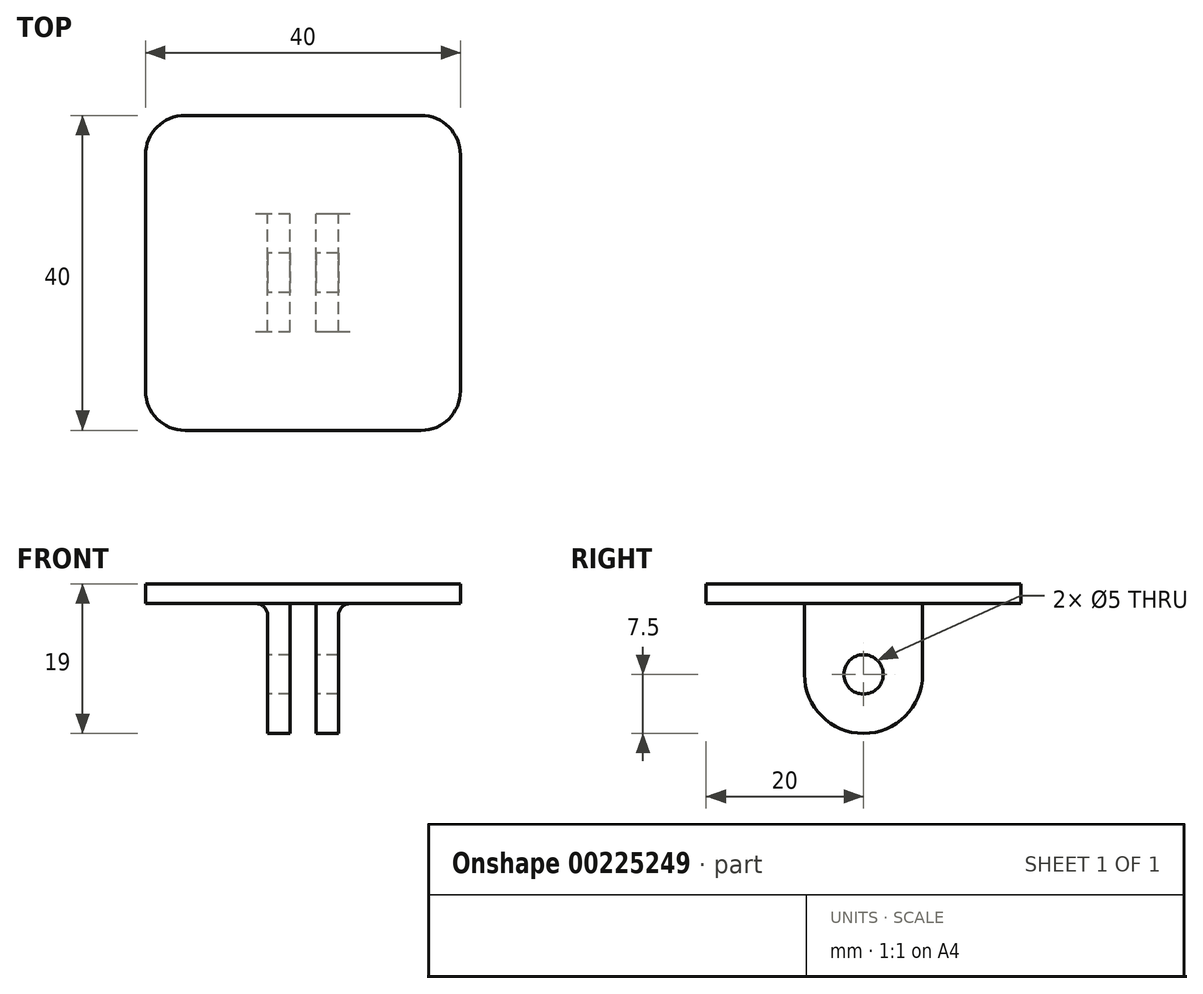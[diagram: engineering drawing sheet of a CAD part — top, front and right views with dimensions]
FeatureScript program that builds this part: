
annotation { "Feature Type Name" : "Feature", "Feature Type Description" : "" }
export const myFeature = defineFeature(function(context is Context, id is Id, definition is map)
    precondition{}
    {
        {
            var Q0;
            Q0=qCreatedBy(makeId("Right.planeOp"),FACE);
            var sketch = newSketch(context, id + "F0", { "sketchPlane" : qUnion([Q0])});
            skArc(sketch, "E0", {"start": v(-7.5, 0) * mm, "mid": v(0, -7.5) * mm, "end": v(7.5, 0) * mm});
            skLineSegment(sketch, "E1", {"start": v(-7.5, 0) * mm, "end": v(-7.5, 9) * mm});
            skLineSegment(sketch, "E2", {"start": v(-7.5, 9) * mm, "end": v(-20, 9) * mm});
            skLineSegment(sketch, "E3", {"start": v(-20, 9) * mm, "end": v(-20, 11.5) * mm});
            skLineSegment(sketch, "E4", {"start": v(-20, 11.5) * mm, "end": v(20, 11.5) * mm});
            skLineSegment(sketch, "E5", {"start": v(7.5, 0) * mm, "end": v(7.5, 9) * mm});
            skLineSegment(sketch, "E6", {"start": v(7.5, 9) * mm, "end": v(20, 9) * mm});
            skLineSegment(sketch, "E7", {"start": v(20, 9) * mm, "end": v(20, 11.5) * mm});
            skCircle(sketch, "E8", {"center": v(0, 0) * mm, "radius": 2.5 * mm});
            skLineSegment(sketch, "E9", {"start": v(-7.5, 9) * mm, "end": v(7.5, 9) * mm});
            skSolve(sketch);
        }
        {
            var Q0;
            Q0=qSketchRegion(id+"F0",true);
            extrude(context, id + "F1", {"entities" : qUnion([Q0]), "depth" : 9 * mm, "symmetric" : true});
        }
        {
            var Q0;
            Q0=makeQuery(id+"F0.imprint","IMPRINT",FACE,{"disambiguationData":[TD([[makeQuery(id+"F0.imprint","IMPRINT",EDGE,{"derivedFrom":sQuery(id+"F0.wireOp",EDGE,"E2")}),-1.0]])]});
            extrude(context, id + "F2", {"entities" : qUnion([Q0]), "operationType" : NewBodyOperationType.ADD, "depth" : 40 * mm, "symmetric" : true});
        }
        {
            var Q0;
            {var subQ0=sQuery(id+"F0.wireOp",EDGE,"E6");var subQ1=sQuery(id+"F0.wireOp",EDGE,"E2");Q0=makeQuery(id+"F2.boolean.opBoolean","MERGE",FACE,{"derivedFrom":[makeQuery(id+"F1.opExtrude","SWEPT_FACE",FACE,{"disambiguationData":[OSD([subQ1])]}),makeQuery(id+"F1.opExtrude","SWEPT_FACE",FACE,{"disambiguationData":[OSD([subQ0])]}),makeQuery(id+"F2.opExtrude","SWEPT_FACE",FACE,{"disambiguationData":[OSD([subQ1,subQ0,sQuery(id+"F0.wireOp",EDGE,"E9")])]})]});}
            var sketch = newSketch(context, id + "F3", { "sketchPlane" : qUnion([Q0])});
            skLineSegment(sketch, "E10.bottom", {"start": v(1.63, 10) * mm, "end": v(-1.62, 10) * mm});
            skLineSegment(sketch, "E10.top", {"start": v(1.63, -10) * mm, "end": v(-1.63, -10) * mm});
            skLineSegment(sketch, "E10.left", {"start": v(1.63, 10) * mm, "end": v(1.63, -10) * mm});
            skLineSegment(sketch, "E10.right", {"start": v(-1.62, 10) * mm, "end": v(-1.63, -10) * mm});
            skPoint(sketch, "E10.middle", {"position": v(0, 0) * mm});
            skSolve(sketch);
        }
        {
            var Q0;
            Q0=qSketchRegion(id+"F3",true);
            extrude(context, id + "F4", {"entities" : qUnion([Q0]), "operationType" : NewBodyOperationType.REMOVE, "depth" : 25 * mm});
        }
        {
            var Q0;
            {var subQ0=sQuery(id+"F0.wireOp",EDGE,"E6");var subQ1=sQuery(id+"F0.wireOp",EDGE,"E2");Q0=makeQuery(id+"F2.boolean.opBoolean","INTERSECT",EDGE,{"derivedFrom":[makeQuery(id+"F1.opExtrude","CAP_FACE",FACE,{"disambiguationData":[OSD([sQuery(id+"F0.wireOp",EDGE,"E0"),sQuery(id+"F0.wireOp",EDGE,"E1"),subQ1,sQuery(id+"F0.wireOp",EDGE,"E3"),sQuery(id+"F0.wireOp",EDGE,"E4"),sQuery(id+"F0.wireOp",EDGE,"E5"),subQ0,sQuery(id+"F0.wireOp",EDGE,"E7"),sQuery(id+"F0.wireOp",EDGE,"E8")])],"isStart":true}),makeQuery(id+"F2.opExtrude","SWEPT_FACE",FACE,{"disambiguationData":[OSD([subQ1,subQ0,sQuery(id+"F0.wireOp",EDGE,"E9")])]})]});}
            var Q1;
            {var subQ0=sQuery(id+"F0.wireOp",EDGE,"E6");var subQ1=sQuery(id+"F0.wireOp",EDGE,"E2");Q1=makeQuery(id+"F2.boolean.opBoolean","INTERSECT",EDGE,{"derivedFrom":[makeQuery(id+"F1.opExtrude","CAP_FACE",FACE,{"disambiguationData":[OSD([sQuery(id+"F0.wireOp",EDGE,"E0"),sQuery(id+"F0.wireOp",EDGE,"E1"),subQ1,sQuery(id+"F0.wireOp",EDGE,"E3"),sQuery(id+"F0.wireOp",EDGE,"E4"),sQuery(id+"F0.wireOp",EDGE,"E5"),subQ0,sQuery(id+"F0.wireOp",EDGE,"E7"),sQuery(id+"F0.wireOp",EDGE,"E8")])],"isStart":false}),makeQuery(id+"F2.opExtrude","SWEPT_FACE",FACE,{"disambiguationData":[OSD([subQ1,subQ0,sQuery(id+"F0.wireOp",EDGE,"E9")])]})]});}
            var Q2;
            {var subQ0=sQuery(id+"F0.wireOp",EDGE,"E6");var subQ1=sQuery(id+"F0.wireOp",EDGE,"E5");var subQ3=sQuery(id+"F0.wireOp",EDGE,"E9");var subQ4=sQuery(id+"F3.wireOp",EDGE,"E10.right");Q2=makeQuery(id+"F4.boolean.opBoolean","SPLIT",EDGE,{"disambiguationData":[TD([makeQuery(id+"F4.opExtrude","SWEPT_FACE",FACE,{"disambiguationData":[OSD([subQ4])]})])],"derivedFrom":makeQuery(id+"F1.opExtrude","SWEPT_EDGE",EDGE,{"disambiguationData":[OSD([subQ1,subQ0,subQ3])]})});}
            var Q3;
            {var subQ0=sQuery(id+"F0.wireOp",EDGE,"E5");var subQ2=sQuery(id+"F0.wireOp",EDGE,"E6");var subQ3=sQuery(id+"F0.wireOp",EDGE,"E9");var subQ4=sQuery(id+"F3.wireOp",EDGE,"E10.left");Q3=makeQuery(id+"F4.boolean.opBoolean","SPLIT",EDGE,{"disambiguationData":[TD([makeQuery(id+"F4.opExtrude","SWEPT_FACE",FACE,{"disambiguationData":[OSD([subQ4])]})])],"derivedFrom":makeQuery(id+"F1.opExtrude","SWEPT_EDGE",EDGE,{"disambiguationData":[OSD([subQ0,subQ2,subQ3])]})});}
            var Q4;
            {var subQ0=sQuery(id+"F0.wireOp",EDGE,"E2");var subQ2=sQuery(id+"F0.wireOp",EDGE,"E1");var subQ3=sQuery(id+"F0.wireOp",EDGE,"E9");var subQ4=sQuery(id+"F3.wireOp",EDGE,"E10.left");Q4=makeQuery(id+"F4.boolean.opBoolean","SPLIT",EDGE,{"disambiguationData":[TD([makeQuery(id+"F4.opExtrude","SWEPT_FACE",FACE,{"disambiguationData":[OSD([subQ4])]})])],"derivedFrom":makeQuery(id+"F1.opExtrude","SWEPT_EDGE",EDGE,{"disambiguationData":[OSD([subQ2,subQ0,subQ3])]})});}
            var Q5;
            {var subQ0=sQuery(id+"F0.wireOp",EDGE,"E2");var subQ2=sQuery(id+"F0.wireOp",EDGE,"E1");var subQ3=sQuery(id+"F3.wireOp",EDGE,"E10.right");var subQ4=sQuery(id+"F0.wireOp",EDGE,"E9");Q5=makeQuery(id+"F4.boolean.opBoolean","SPLIT",EDGE,{"disambiguationData":[TD([makeQuery(id+"F4.opExtrude","SWEPT_FACE",FACE,{"disambiguationData":[OSD([subQ3])]})])],"derivedFrom":makeQuery(id+"F1.opExtrude","SWEPT_EDGE",EDGE,{"disambiguationData":[OSD([subQ2,subQ0,subQ4])]})});}
            fillet(context, id + "F5", {"entities" : qUnion([Q0, Q1, Q2, Q3, Q4, Q5]), "radius" : 1.5 * mm, "allowEdgeOverflow" : false});
        }
        {
            var Q0;
            Q0=makeQuery(id+"F2.opExtrude","CAP_EDGE",EDGE,{"disambiguationData":[OSD([sQuery(id+"F0.wireOp",EDGE,"E3")])],"isStart":false});
            var Q1;
            Q1=makeQuery(id+"F2.opExtrude","CAP_EDGE",EDGE,{"disambiguationData":[OSD([sQuery(id+"F0.wireOp",EDGE,"E3")])],"isStart":true});
            var Q2;
            Q2=makeQuery(id+"F2.opExtrude","CAP_EDGE",EDGE,{"disambiguationData":[OSD([sQuery(id+"F0.wireOp",EDGE,"E7")])],"isStart":false});
            var Q3;
            Q3=makeQuery(id+"F2.opExtrude","CAP_EDGE",EDGE,{"disambiguationData":[OSD([sQuery(id+"F0.wireOp",EDGE,"E7")])],"isStart":true});
            fillet(context, id + "F6", {"entities" : qUnion([Q0, Q1, Q2, Q3]), "radius" : 5 * mm, "allowEdgeOverflow" : false});
        }
    });
